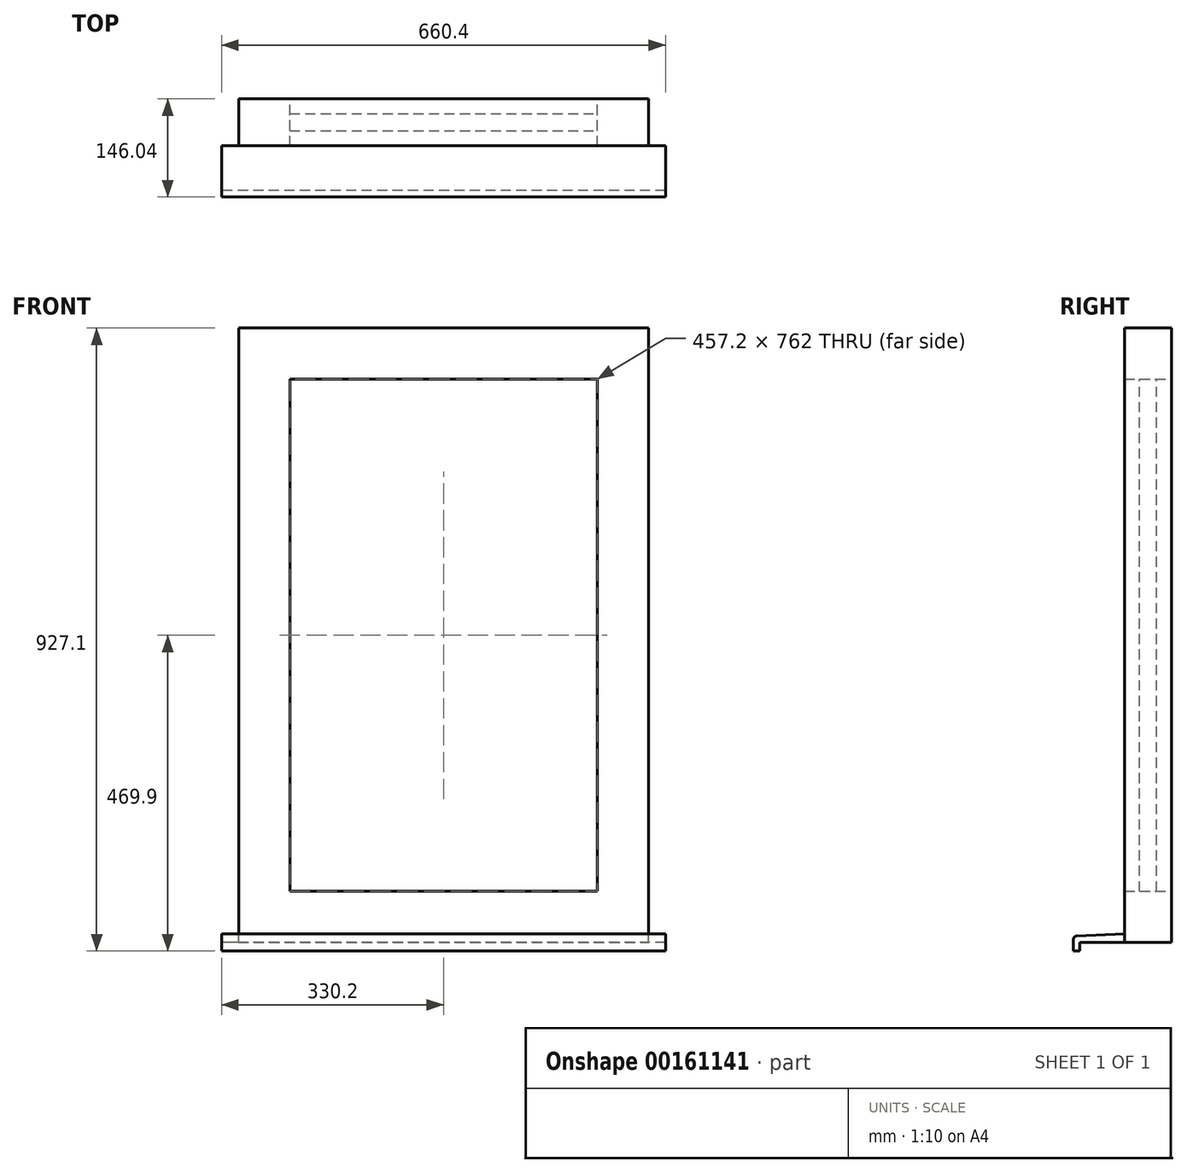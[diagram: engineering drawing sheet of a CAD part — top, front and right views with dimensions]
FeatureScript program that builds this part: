
annotation { "Feature Type Name" : "Feature", "Feature Type Description" : "" }
export const myFeature = defineFeature(function(context is Context, id is Id, definition is map)
    precondition{}
    {
        {
            var Q0;
            Q0=qCreatedBy(makeId("Front.planeOp"),FACE);
            var sketch = newSketch(context, id + "F0", { "sketchPlane" : qUnion([Q0])});
            skLineSegment(sketch, "E0.bottom", {"start": v(0, 0) * mm, "end": v(609.6, 0) * mm});
            skLineSegment(sketch, "E0.top", {"start": v(0, 914.4) * mm, "end": v(609.6, 914.4) * mm});
            skLineSegment(sketch, "E0.left", {"start": v(0, 0) * mm, "end": v(0, 914.4) * mm});
            skLineSegment(sketch, "E0.right", {"start": v(609.6, 0) * mm, "end": v(609.6, 914.4) * mm});
            skLineSegment(sketch, "E1.bottom", {"start": v(76.2, 838.2) * mm, "end": v(533.4, 838.2) * mm});
            skLineSegment(sketch, "E1.top", {"start": v(76.2, 76.2) * mm, "end": v(533.4, 76.2) * mm});
            skLineSegment(sketch, "E1.left", {"start": v(76.2, 838.2) * mm, "end": v(76.2, 76.2) * mm});
            skLineSegment(sketch, "E1.right", {"start": v(533.4, 838.2) * mm, "end": v(533.4, 76.2) * mm});
            skSolve(sketch);
        }
        {
            var Q0;
            Q0=qSketchRegion(id+"F0",true);
            extrude(context, id + "F1", {"entities" : qUnion([Q0]), "endBound" : BoundingType.SYMMETRIC, "depth" : 69.85 * mm});
        }
        {
            var Q0;
            Q0=qCreatedBy(makeId("Front.planeOp"),FACE);
            var sketch = newSketch(context, id + "F2", { "sketchPlane" : qUnion([Q0])});
            skLineSegment(sketch, "E2.bottom", {"start": v(76.2, 76.2) * mm, "end": v(533.4, 76.2) * mm});
            skLineSegment(sketch, "E2.top", {"start": v(76.2, 838.2) * mm, "end": v(533.4, 838.2) * mm});
            skLineSegment(sketch, "E2.left", {"start": v(76.2, 76.2) * mm, "end": v(76.2, 838.2) * mm});
            skLineSegment(sketch, "E2.right", {"start": v(533.4, 76.2) * mm, "end": v(533.4, 838.2) * mm});
            skSolve(sketch);
        }
        {
            var Q0;
            Q0=qSketchRegion(id+"F2",true);
            extrude(context, id + "F3", {"entities" : qUnion([Q0]), "endBound" : BoundingType.SYMMETRIC, "depth" : 25.4 * mm});
        }
        {
            var Q0;
            Q0=makeQuery(id+"F1.opExtrude","SWEPT_FACE",FACE,{"disambiguationData":[OSD([sQuery(id+"F0.wireOp",EDGE,"E0.left")])]});
            var sketch = newSketch(context, id + "F4", { "sketchPlane" : qUnion([Q0])});
            skLineSegment(sketch, "E3", {"start": v(34.93, 0) * mm, "end": v(34.93, 12.7) * mm});
            skLineSegment(sketch, "E4", {"start": v(34.92, 12.7) * mm, "end": v(111.12, 9.53) * mm});
            skLineSegment(sketch, "E5", {"start": v(111.12, 9.53) * mm, "end": v(111.12, -12.7) * mm});
            skLineSegment(sketch, "E6", {"start": v(111.12, -12.7) * mm, "end": v(101.6, -12.7) * mm});
            skLineSegment(sketch, "E7", {"start": v(101.6, -12.7) * mm, "end": v(101.6, 0) * mm});
            skLineSegment(sketch, "E8", {"start": v(101.6, 0) * mm, "end": v(34.93, 0) * mm});
            skSolve(sketch);
        }
        {
            var Q0;
            Q0=qSketchRegion(id+"F4",true);
            extrude(context, id + "F5", {"entities" : qUnion([Q0]), "operationType" : NewBodyOperationType.ADD, "oppositeDirection" : true, "depth" : 635 * mm, "hasSecondDirection" : true, "secondDirectionOppositeDirection" : false, "secondDirectionDepth" : 25.4 * mm});
        }
        {
            var Q0;
            Q0=makeQuery(id+"F5.opExtrude","SWEPT_EDGE",EDGE,{"disambiguationData":[OSD([sQuery(id+"F4.wireOp",EDGE,"E4"),sQuery(id+"F4.wireOp",EDGE,"E5")])]});
            fillet(context, id + "F6", {"entities" : qUnion([Q0]), "radius" : 5.08 * mm, "tangentPropagation" : true, "allowEdgeOverflow" : false});
        }
    });
